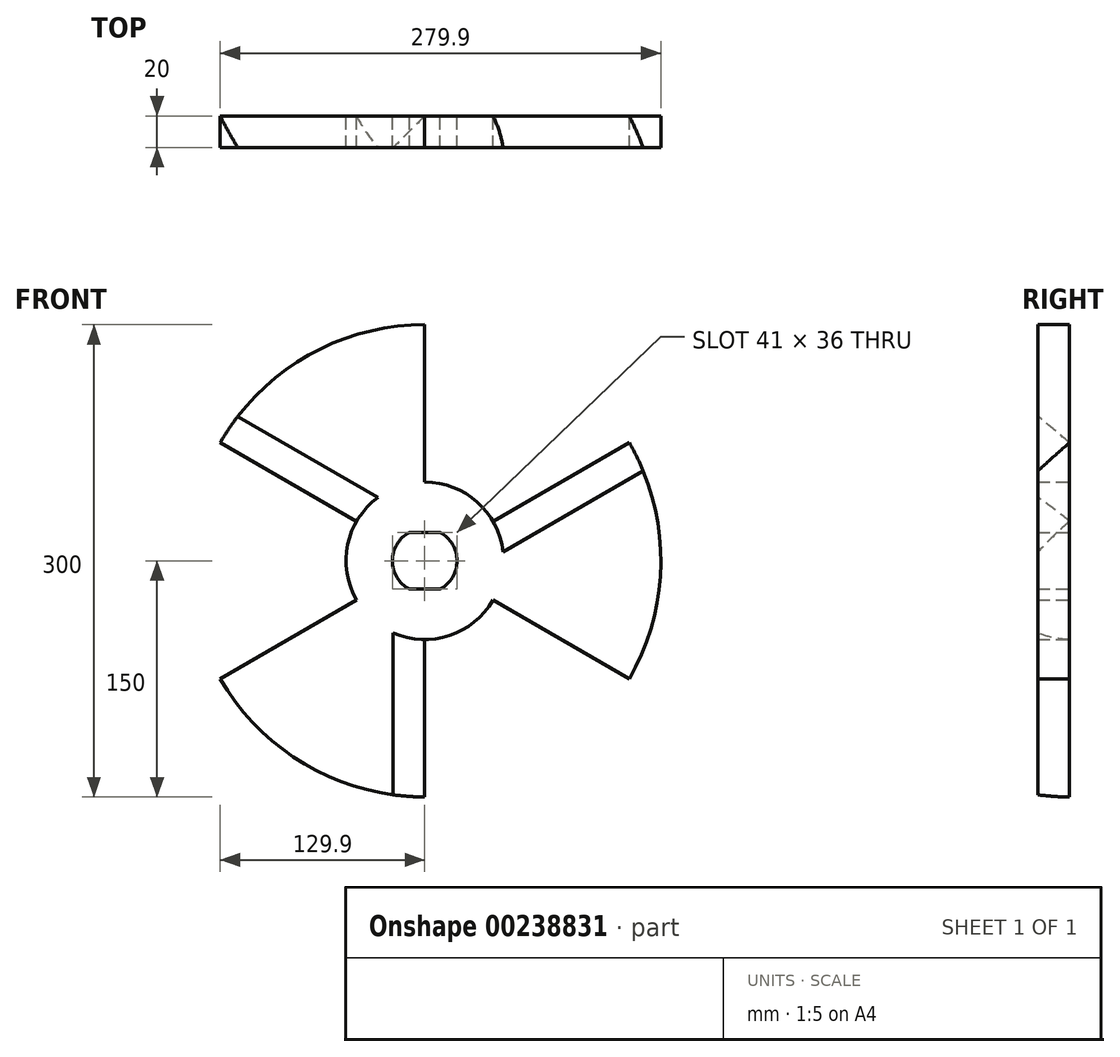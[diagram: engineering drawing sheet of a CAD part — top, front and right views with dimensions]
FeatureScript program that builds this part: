
annotation { "Feature Type Name" : "Feature", "Feature Type Description" : "" }
export const myFeature = defineFeature(function(context is Context, id is Id, definition is map)
    precondition{}
    {
        {
            var Q0;
            Q0=qCreatedBy(makeId("Front.planeOp"),FACE);
            var sketch = newSketch(context, id + "F0", { "sketchPlane" : qUnion([Q0])});
            skArc(sketch, "E0", {"start": v(-9.81, 18) * mm, "mid": v(-20.5, 0) * mm, "end": v(-9.81, -18) * mm});
            skArc(sketch, "E1", {"start": v(-43.3, 25) * mm, "mid": v(-50, 0) * mm, "end": v(-43.3, -25) * mm});
            skArc(sketch, "E2", {"start": v(0, 150) * mm, "mid": v(-75, 129.9) * mm, "end": v(-129.9, 75) * mm});
            skLineSegment(sketch, "E3", {"start": v(0, 50) * mm, "end": v(0, 150) * mm});
            skLineSegment(sketch, "E4.1.0", {"start": v(-43.3, 25) * mm, "end": v(-129.9, 75) * mm});
            skLineSegment(sketch, "E4.2.0", {"start": v(-43.3, -25) * mm, "end": v(-129.9, -75) * mm});
            skLineSegment(sketch, "E4.3.0", {"start": v(0, -50) * mm, "end": v(0, -150) * mm});
            skLineSegment(sketch, "E4.4.0", {"start": v(43.3, -25) * mm, "end": v(129.9, -75) * mm});
            skLineSegment(sketch, "E4.5.0", {"start": v(43.3, 25) * mm, "end": v(129.9, 75) * mm});
            skArc(sketch, "E5.trimOffspring", {"start": v(-129.9, -75) * mm, "mid": v(-75, -129.9) * mm, "end": v(0, -150) * mm});
            skArc(sketch, "E6.trimOffspring", {"start": v(0, -50) * mm, "mid": v(25, -43.3) * mm, "end": v(43.3, -25) * mm});
            skArc(sketch, "E7.trimOffspring", {"start": v(129.9, -75) * mm, "mid": v(150, 0) * mm, "end": v(129.9, 75) * mm});
            skArc(sketch, "E8.trimOffspring", {"start": v(43.3, 25) * mm, "mid": v(25, 43.3) * mm, "end": v(0, 50) * mm});
            skLineSegment(sketch, "E9", {"start": v(-9.81, 18) * mm, "end": v(9.81, 18) * mm});
            skLineSegment(sketch, "E10", {"start": v(-9.81, -18) * mm, "end": v(9.81, -18) * mm});
            skArc(sketch, "E11.trimOffspring", {"start": v(9.81, -18) * mm, "mid": v(20.5, 0) * mm, "end": v(9.81, 18) * mm});
            skSolve(sketch);
        }
        {
            var Q0;
            Q0=makeQuery(id+"F0.imprint","IMPRINT",FACE,{"disambiguationData":[TD([[makeQuery(id+"F0.imprint","IMPRINT",EDGE,{"derivedFrom":sQuery(id+"F0.wireOp",EDGE,"E0")}),-1.0]])]});
            extrude(context, id + "F1", {"entities" : qUnion([Q0]), "depth" : 20 * mm});
        }
        {
            var Q0;
            Q0=makeQuery(id+"F1.opExtrude","CAP_EDGE",EDGE,{"disambiguationData":[OSD([sQuery(id+"F0.wireOp",EDGE,"E4.1.0")])],"isStart":false});
            var Q1;
            Q1=makeQuery(id+"F1.opExtrude","CAP_EDGE",EDGE,{"disambiguationData":[OSD([sQuery(id+"F0.wireOp",EDGE,"E4.3.0")])],"isStart":false});
            var Q2;
            Q2=makeQuery(id+"F1.opExtrude","CAP_EDGE",EDGE,{"disambiguationData":[OSD([sQuery(id+"F0.wireOp",EDGE,"E4.5.0")])],"isStart":false});
            chamfer(context, id + "F2", {"entities" : qUnion([Q0, Q1, Q2]), "width" : 20 * mm, "tangentPropagation" : true});
        }
    });
